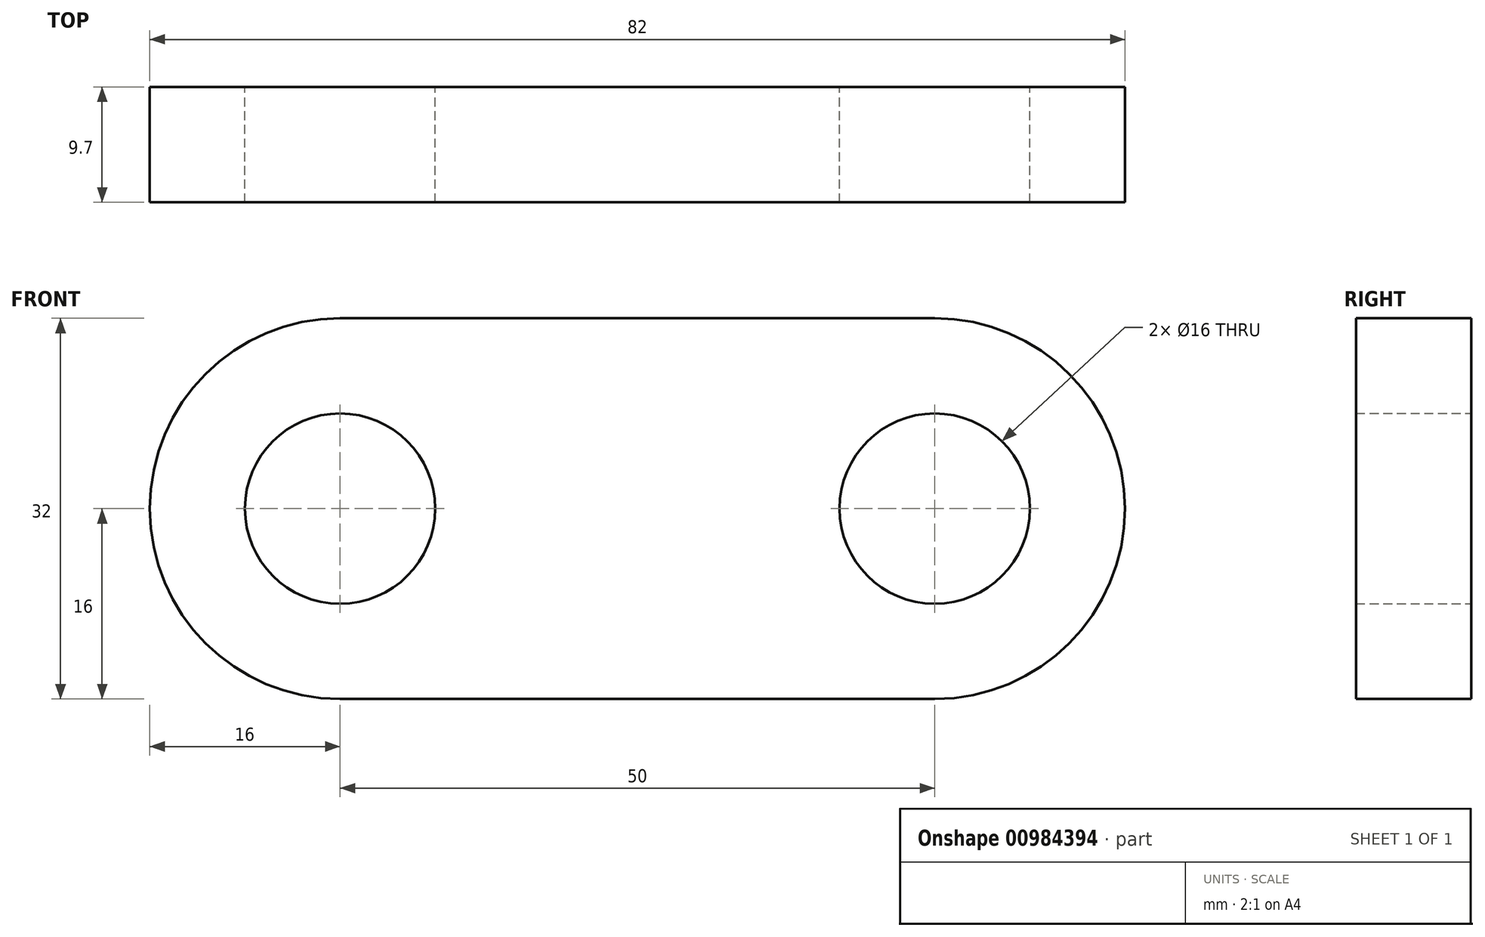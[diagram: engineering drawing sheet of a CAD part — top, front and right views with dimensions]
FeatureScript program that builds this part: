
annotation { "Feature Type Name" : "Feature", "Feature Type Description" : "" }
export const myFeature = defineFeature(function(context is Context, id is Id, definition is map)
    precondition{}
    {
        {
            var Q0;
            Q0=qCreatedBy(makeId("Front.planeOp"),FACE);
            var sketch = newSketch(context, id + "F0", { "sketchPlane" : qUnion([Q0])});
            skLineSegment(sketch, "E0", {"start": v(-25, 16) * mm, "end": v(25, 16) * mm});
            skLineSegment(sketch, "E1", {"start": v(25, -16) * mm, "end": v(-25, -16) * mm});
            skLineSegment(sketch, "E2", {"start": v(-67.25, 0) * mm, "end": v(95.23, 0) * mm, "construction": true});
            skLineSegment(sketch, "E3", {"start": v(0, 68.76) * mm, "end": v(0, -60.15) * mm, "construction": true});
            skCircle(sketch, "E4", {"center": v(-25, 0) * mm, "radius": 8 * mm});
            skCircle(sketch, "E5.MirrorC", {"center": v(25, 0) * mm, "radius": 8 * mm});
            skArc(sketch, "E6", {"start": v(-25, 16) * mm, "mid": v(-41, 0) * mm, "end": v(-25, -16) * mm});
            skArc(sketch, "E7", {"start": v(25, -16) * mm, "mid": v(41, 0) * mm, "end": v(25, 16) * mm});
            skSolve(sketch);
        }
        {
            var Q0;
            Q0=makeQuery(id+"F0.imprint","IMPRINT",FACE,{"disambiguationData":[TD([[makeQuery(id+"F0.imprint","IMPRINT",EDGE,{"derivedFrom":sQuery(id+"F0.wireOp",EDGE,"E0")}),-1.0]])]});
            extrude(context, id + "F1", {"entities" : qUnion([Q0]), "depth" : 9.7 * mm, "offsetDistance" : 25 * mm});
        }
    });
